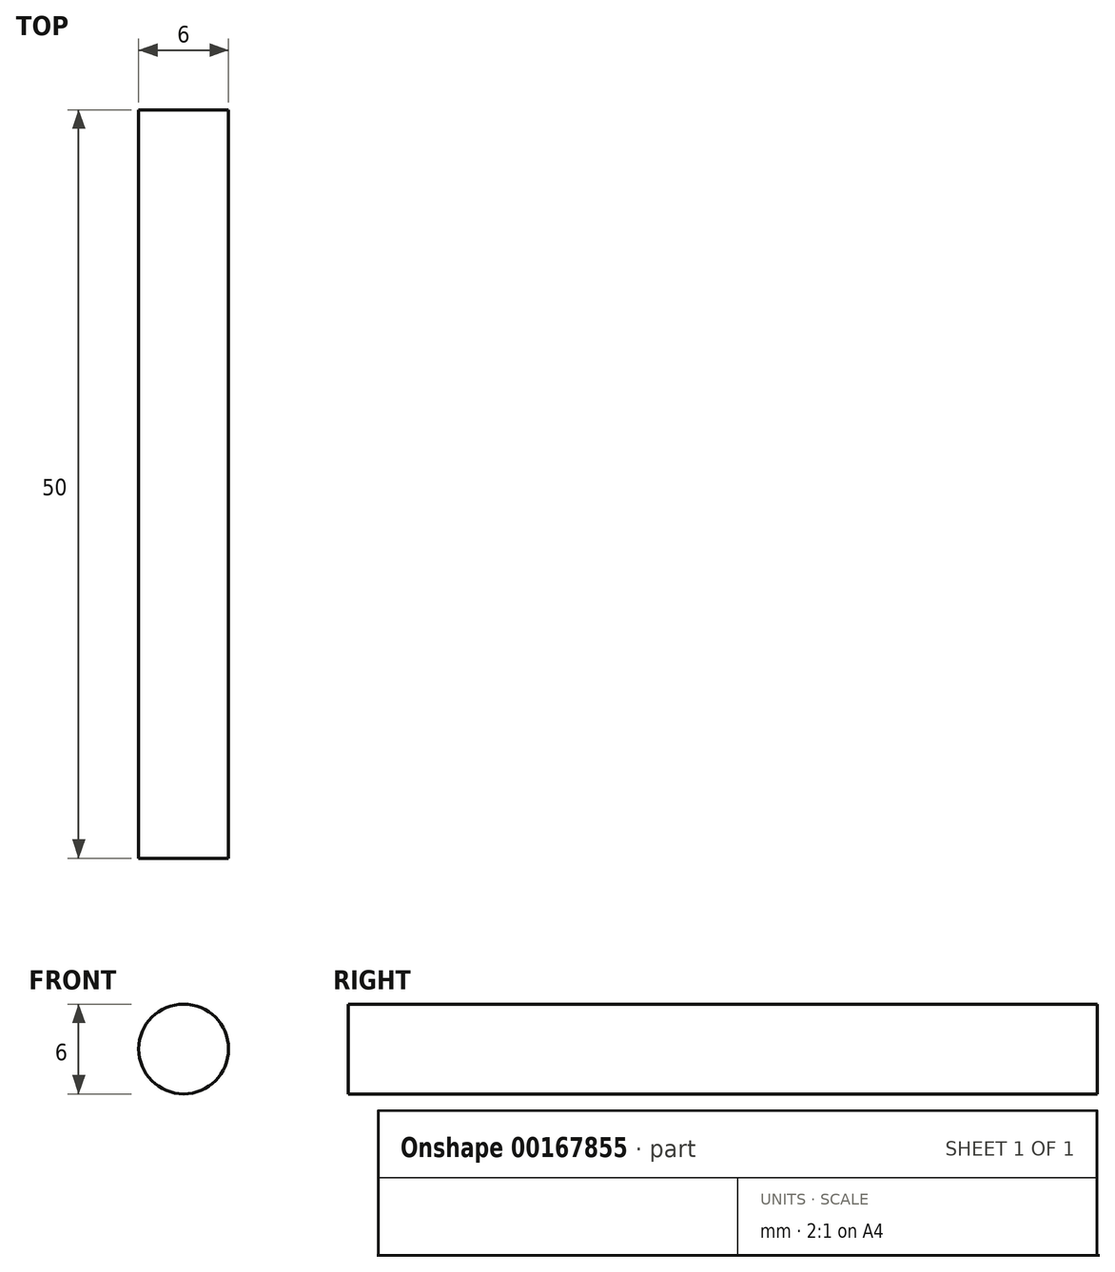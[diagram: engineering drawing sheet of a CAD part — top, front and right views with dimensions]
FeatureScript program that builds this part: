
annotation { "Feature Type Name" : "Feature", "Feature Type Description" : "" }
export const myFeature = defineFeature(function(context is Context, id is Id, definition is map)
    precondition{}
    {
        {
            var Q0;
            Q0=qCreatedBy(makeId("Front.planeOp"),FACE);
            var sketch = newSketch(context, id + "F0", { "sketchPlane" : qUnion([Q0])});
            skCircle(sketch, "E0", {"center": v(0, 0) * mm, "radius": 3 * mm});
            skSolve(sketch);
        }
        {
            var Q0;
            Q0 = qSketchRegion(id + "F0", true);
            extrude(context, id + "F1", {"entities" : qUnion([Q0]), "depth" : 50 * mm});
        }
    });
